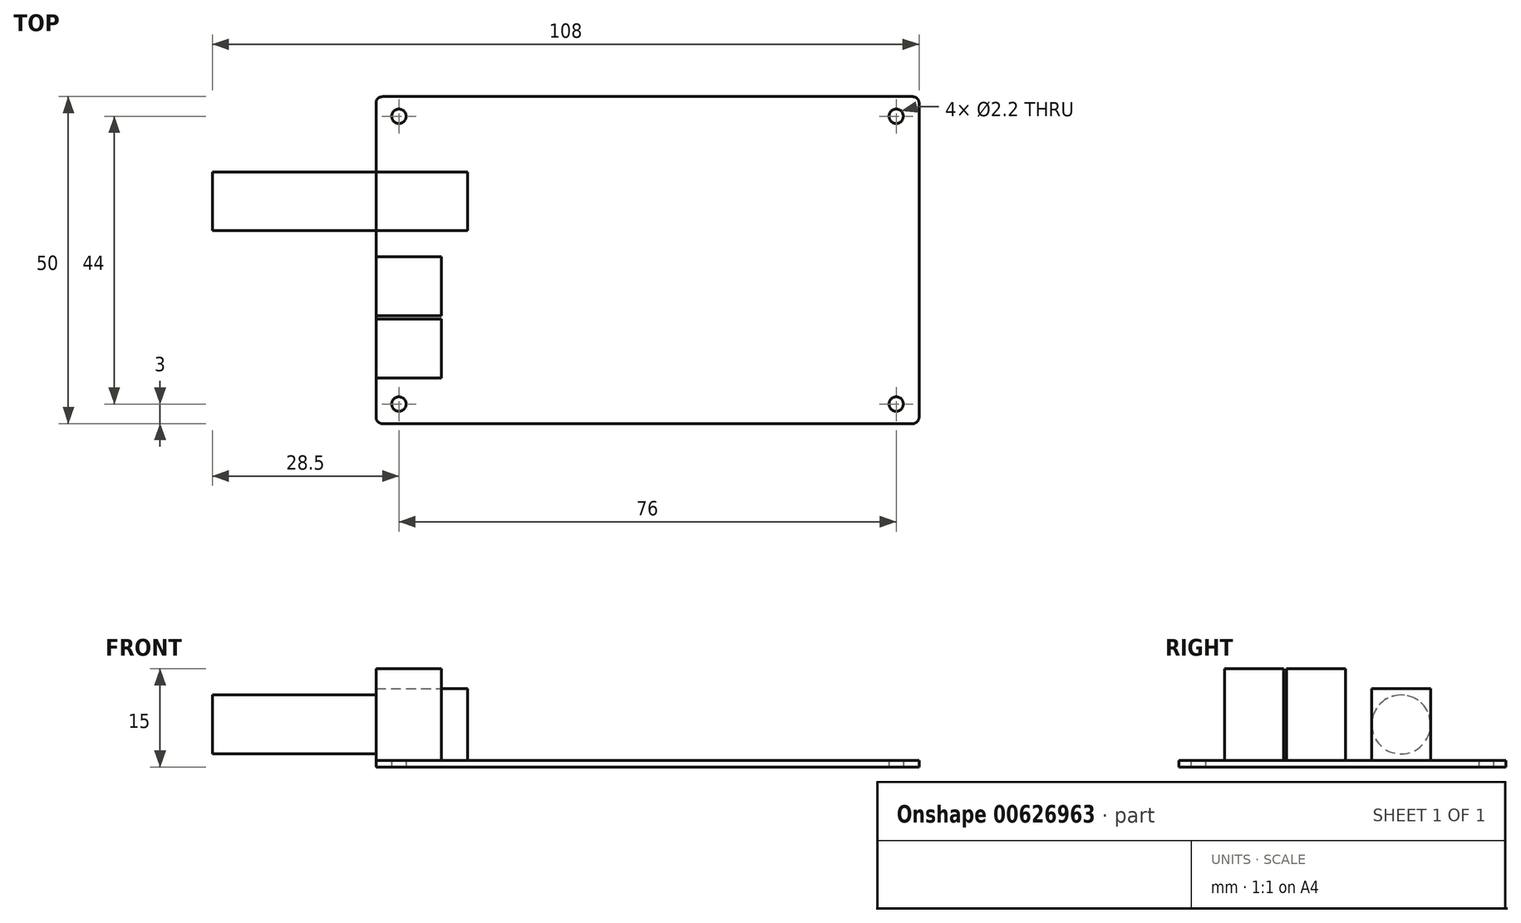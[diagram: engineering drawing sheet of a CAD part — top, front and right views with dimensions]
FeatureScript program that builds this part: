
annotation { "Feature Type Name" : "Feature", "Feature Type Description" : "" }
export const myFeature = defineFeature(function(context is Context, id is Id, definition is map)
    precondition{}
    {
        {
            var Q0;
            Q0=qCreatedBy(makeId("Top.planeOp"),FACE);
            var sketch = newSketch(context, id + "F0", { "sketchPlane" : qUnion([Q0])});
            skLineSegment(sketch, "E0.bottom", {"start": v(1, 0) * mm, "end": v(82, 0) * mm});
            skLineSegment(sketch, "E0.top", {"start": v(1, 50) * mm, "end": v(82, 50) * mm});
            skLineSegment(sketch, "E0.left", {"start": v(0, 1) * mm, "end": v(0, 49) * mm});
            skLineSegment(sketch, "E0.right", {"start": v(83, 1) * mm, "end": v(83, 49) * mm});
            skPoint(sketch, "E1", {"position": v(3.5, 47) * mm});
            skPoint(sketch, "E2", {"position": v(79.5, 47) * mm});
            skPoint(sketch, "E3", {"position": v(79.5, 3) * mm});
            skPoint(sketch, "E4", {"position": v(3.5, 3) * mm});
            skLineSegment(sketch, "E5", {"start": v(3.5, 47) * mm, "end": v(3.5, 50) * mm, "construction": true});
            skLineSegment(sketch, "E6", {"start": v(3.5, 3) * mm, "end": v(3.5, 0) * mm, "construction": true});
            skLineSegment(sketch, "E7", {"start": v(3.5, 3) * mm, "end": v(0, 3) * mm, "construction": true});
            skLineSegment(sketch, "E8", {"start": v(79.5, 3) * mm, "end": v(83, 3) * mm, "construction": true});
            skPoint(sketch, "E9.visualSharp", {"position": v(83, 50) * mm});
            skArc(sketch, "E9.filletArc", {"start": v(83, 49) * mm, "mid": v(82.7, 49.7) * mm, "end": v(82, 50) * mm});
            skPoint(sketch, "E10.visualSharp", {"position": v(83, 0) * mm});
            skArc(sketch, "E10.filletArc", {"start": v(82, 0) * mm, "mid": v(82.7, 0.3) * mm, "end": v(83, 1) * mm});
            skPoint(sketch, "E11.visualSharp", {"position": v(0, 0) * mm});
            skArc(sketch, "E11.filletArc", {"start": v(0, 1) * mm, "mid": v(0.3, 0.3) * mm, "end": v(1, 0) * mm});
            skPoint(sketch, "E12.visualSharp", {"position": v(0, 50) * mm});
            skArc(sketch, "E12.filletArc", {"start": v(1, 50) * mm, "mid": v(0.3, 49.7) * mm, "end": v(0, 49) * mm});
            skCircle(sketch, "E13", {"center": v(3.5, 47) * mm, "radius": 1.1 * mm});
            skCircle(sketch, "E14", {"center": v(3.5, 3) * mm, "radius": 1.1 * mm});
            skCircle(sketch, "E15", {"center": v(79.5, 3) * mm, "radius": 1.1 * mm});
            skCircle(sketch, "E16", {"center": v(79.5, 47) * mm, "radius": 1.1 * mm});
            skSolve(sketch);
        }
        {
            var Q0;
            Q0=makeQuery(id+"F0.imprint","IMPRINT",FACE,{"disambiguationData":[TD([[makeQuery(id+"F0.imprint","IMPRINT",EDGE,{"derivedFrom":sQuery(id+"F0.wireOp",EDGE,"E0.bottom")}),1.0]])]});
            extrude(context, id + "F1", {"entities" : qUnion([Q0]), "depth" : 1 * mm, "offsetDistance" : 25 * mm});
        }
        {
            var Q0;
            Q0=makeQuery(id+"F1.opExtrude","CAP_FACE",FACE,{"disambiguationData":[OSD([sQuery(id+"F0.wireOp",EDGE,"E0.bottom"),sQuery(id+"F0.wireOp",EDGE,"E0.top"),sQuery(id+"F0.wireOp",EDGE,"E0.left"),sQuery(id+"F0.wireOp",EDGE,"E0.right"),sQuery(id+"F0.wireOp",EDGE,"E9.filletArc"),sQuery(id+"F0.wireOp",EDGE,"E10.filletArc"),sQuery(id+"F0.wireOp",EDGE,"E11.filletArc"),sQuery(id+"F0.wireOp",EDGE,"E12.filletArc"),sQuery(id+"F0.wireOp",EDGE,"E13"),sQuery(id+"F0.wireOp",EDGE,"E14"),sQuery(id+"F0.wireOp",EDGE,"E15"),sQuery(id+"F0.wireOp",EDGE,"E16")])],"isStart":false});
            var sketch = newSketch(context, id + "F2", { "sketchPlane" : qUnion([Q0])});
            skLineSegment(sketch, "E17.bottom", {"start": v(0, 7) * mm, "end": v(10, 7) * mm});
            skLineSegment(sketch, "E17.top", {"start": v(0, 16) * mm, "end": v(10, 16) * mm});
            skLineSegment(sketch, "E17.left", {"start": v(0, 7) * mm, "end": v(0, 16) * mm});
            skLineSegment(sketch, "E17.right", {"start": v(10, 7) * mm, "end": v(10, 16) * mm});
            skLineSegment(sketch, "E18.bottom", {"start": v(0, 16.5) * mm, "end": v(10, 16.5) * mm});
            skLineSegment(sketch, "E18.top", {"start": v(0, 25.5) * mm, "end": v(10, 25.5) * mm});
            skLineSegment(sketch, "E18.left", {"start": v(0, 16.5) * mm, "end": v(0, 25.5) * mm});
            skLineSegment(sketch, "E18.right", {"start": v(10, 16.5) * mm, "end": v(10, 25.5) * mm});
            skLineSegment(sketch, "E19.bottom", {"start": v(0, 38.5) * mm, "end": v(14, 38.5) * mm});
            skLineSegment(sketch, "E19.top", {"start": v(0, 29.5) * mm, "end": v(14, 29.5) * mm});
            skLineSegment(sketch, "E19.left", {"start": v(0, 38.5) * mm, "end": v(0, 29.5) * mm});
            skLineSegment(sketch, "E19.right", {"start": v(14, 38.5) * mm, "end": v(14, 29.5) * mm});
            skSolve(sketch);
        }
        {
            var Q0;
            Q0=makeQuery(id+"F2.imprint","IMPRINT",FACE,{"disambiguationData":[TD([[makeQuery(id+"F2.imprint","IMPRINT",EDGE,{"derivedFrom":sQuery(id+"F2.wireOp",EDGE,"E17.bottom")}),1.0]])]});
            var Q1;
            Q1=makeQuery(id+"F2.imprint","IMPRINT",FACE,{"disambiguationData":[TD([[makeQuery(id+"F2.imprint","IMPRINT",EDGE,{"derivedFrom":sQuery(id+"F2.wireOp",EDGE,"E18.bottom")}),1.0]])]});
            extrude(context, id + "F3", {"entities" : qUnion([Q0, Q1]), "operationType" : NewBodyOperationType.ADD, "depth" : 14 * mm, "offsetDistance" : 25 * mm});
        }
        {
            var Q0;
            Q0=makeQuery(id+"F2.imprint","IMPRINT",FACE,{"disambiguationData":[TD([[makeQuery(id+"F2.imprint","IMPRINT",EDGE,{"derivedFrom":sQuery(id+"F2.wireOp",EDGE,"E19.bottom")}),-1.0]])]});
            extrude(context, id + "F4", {"entities" : qUnion([Q0]), "operationType" : NewBodyOperationType.ADD, "depth" : 11 * mm, "offsetDistance" : 25 * mm});
        }
        {
            var Q0;
            Q0=makeQuery(id+"F4.boolean.opBoolean","MERGE",FACE,{"derivedFrom":[makeQuery(id+"F3.boolean.opBoolean","MERGE",FACE,{"derivedFrom":[makeQuery(id+"F1.opExtrude","SWEPT_FACE",FACE,{"disambiguationData":[OSD([sQuery(id+"F0.wireOp",EDGE,"E0.left")])]}),makeQuery(id+"F3.opExtrude","SWEPT_FACE",FACE,{"disambiguationData":[OSD([sQuery(id+"F2.wireOp",EDGE,"E17.left")])]}),makeQuery(id+"F3.opExtrude","SWEPT_FACE",FACE,{"disambiguationData":[OSD([sQuery(id+"F2.wireOp",EDGE,"E18.left")])]})]}),makeQuery(id+"F4.opExtrude","SWEPT_FACE",FACE,{"disambiguationData":[OSD([sQuery(id+"F2.wireOp",EDGE,"E19.left")])]})]});
            var sketch = newSketch(context, id + "F5", { "sketchPlane" : qUnion([Q0])});
            skLineSegment(sketch, "E20", {"start": v(-38.5, 1) * mm, "end": v(-29.5, 1) * mm, "construction": true});
            skPoint(sketch, "E21", {"position": v(-34, 6.5) * mm});
            skPoint(sketch, "E21.positionSnap0", {"position": v(-38.5, 6.5) * mm});
            skPoint(sketch, "E21.positionSnap1", {"position": v(-34, 1) * mm});
            skCircle(sketch, "E22", {"center": v(-34, 6.5) * mm, "radius": 4.5 * mm});
            skSolve(sketch);
        }
        {
            var Q0;
            {var subQ0=sQuery(id+"F5.wireOp",EDGE,"E22");var subQ1=sQuery(id+"F2.wireOp",EDGE,"E19.left");var subQ2=sQuery(id+"F0.wireOp",EDGE,"E0.left");var subQ3=makeQuery(id+"F5.imprint","INTERSECT",VERTEX,{"derivedFrom":[makeQuery(id+"F4.opExtrude","SWEPT_EDGE",EDGE,{"disambiguationData":[OSD([subQ2,sQuery(id+"F2.wireOp",EDGE,"E19.bottom"),subQ1])]}),subQ0]});Q0=makeQuery(id+"F5.imprint","IMPRINT",FACE,{"disambiguationData":[TD([[makeQuery(id+"F5.imprint","IMPRINT",EDGE,{"disambiguationData":[TD([[subQ3,1.0]])],"derivedFrom":subQ0}),1.0]])]});}
            extrude(context, id + "F6", {"entities" : qUnion([Q0]), "operationType" : NewBodyOperationType.ADD, "depth" : 25 * mm, "offsetDistance" : 25 * mm});
        }
    });
